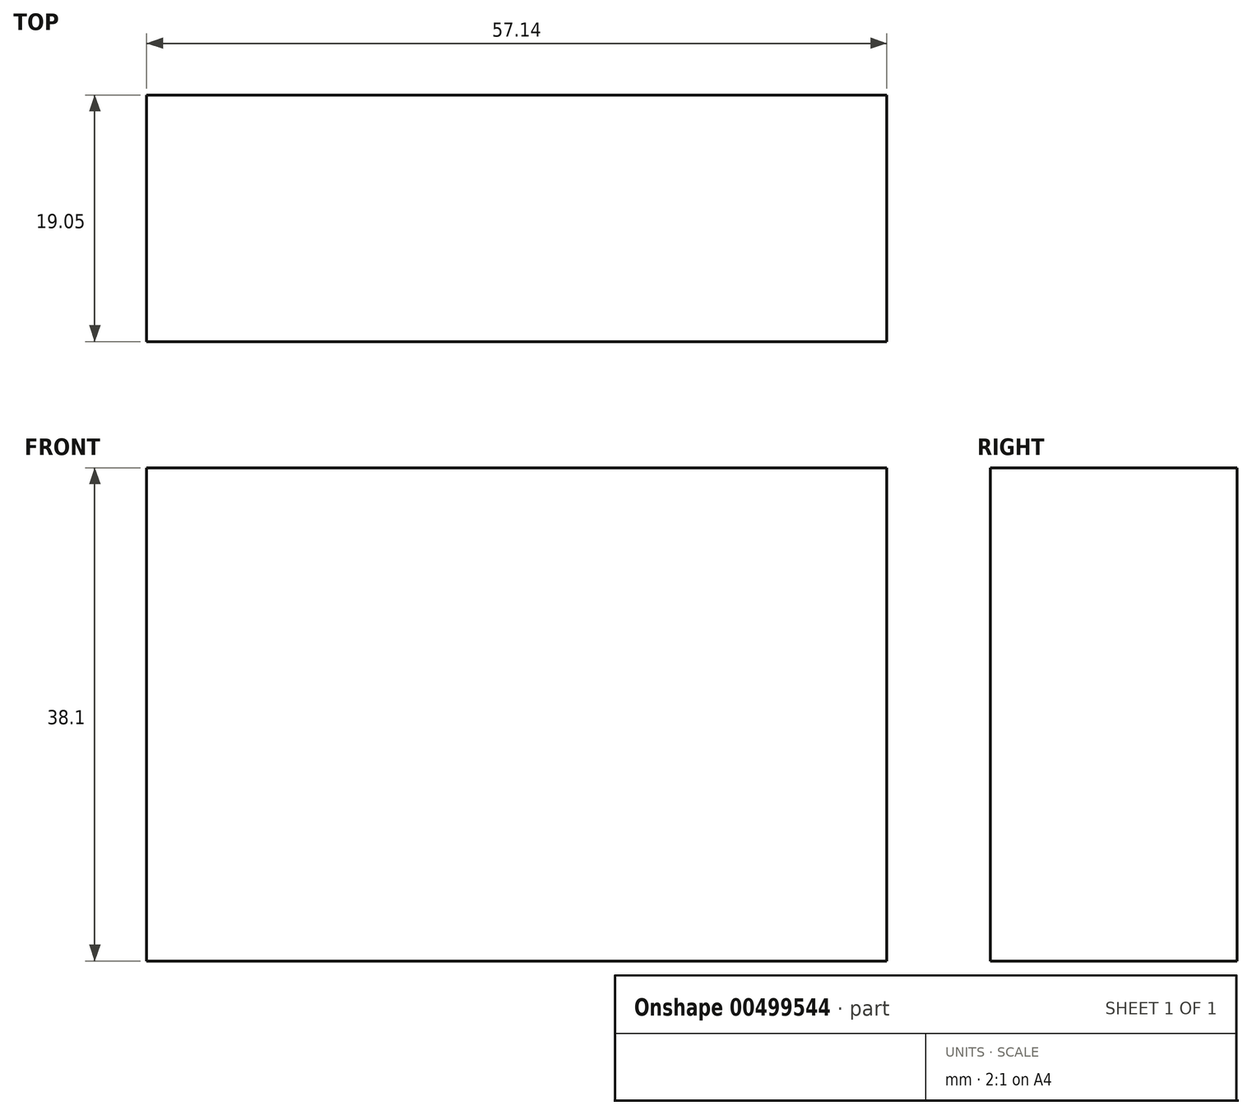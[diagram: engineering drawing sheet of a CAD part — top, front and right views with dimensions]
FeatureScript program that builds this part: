
annotation { "Feature Type Name" : "Feature", "Feature Type Description" : "" }
export const myFeature = defineFeature(function(context is Context, id is Id, definition is map)
    precondition{}
    {
        {
            var Q0;
            Q0=qCreatedBy(makeId("Top.planeOp"),FACE);
            var sketch = newSketch(context, id + "F0", { "sketchPlane" : qUnion([Q0])});
            skLineSegment(sketch, "E0.bottom", {"start": v(-28.58, 19.05) * mm, "end": v(28.58, 19.05) * mm});
            skLineSegment(sketch, "E0.top", {"start": v(-28.58, -19.05) * mm, "end": v(28.58, -19.05) * mm});
            skLineSegment(sketch, "E0.left", {"start": v(-28.58, 19.05) * mm, "end": v(-28.58, -19.05) * mm});
            skLineSegment(sketch, "E0.right", {"start": v(28.58, 19.05) * mm, "end": v(28.57, -19.05) * mm});
            skPoint(sketch, "E0.middle", {"position": v(0, 0) * mm});
            skLineSegment(sketch, "E1.bottom", {"start": v(28.58, -19.05) * mm, "end": v(9.52, -19.05) * mm});
            skLineSegment(sketch, "E1.top", {"start": v(28.58, 0) * mm, "end": v(9.52, 0) * mm});
            skLineSegment(sketch, "E1.left", {"start": v(28.58, -19.05) * mm, "end": v(28.58, 0) * mm});
            skLineSegment(sketch, "E1.right", {"start": v(9.52, -19.05) * mm, "end": v(9.52, 0) * mm});
            skLineSegment(sketch, "E2.bottom", {"start": v(9.52, 0) * mm, "end": v(-9.53, 0) * mm});
            skLineSegment(sketch, "E2.top", {"start": v(9.52, -19.05) * mm, "end": v(-9.53, -19.05) * mm});
            skLineSegment(sketch, "E2.left", {"start": v(9.52, 0) * mm, "end": v(9.52, -19.05) * mm});
            skLineSegment(sketch, "E2.right", {"start": v(-9.53, 0) * mm, "end": v(-9.53, -19.05) * mm});
            skLineSegment(sketch, "E3.bottom", {"start": v(-9.53, 0) * mm, "end": v(-28.58, 0) * mm});
            skLineSegment(sketch, "E3.top", {"start": v(-9.53, -19.05) * mm, "end": v(-28.58, -19.05) * mm});
            skLineSegment(sketch, "E3.right", {"start": v(-28.58, 0) * mm, "end": v(-28.58, -19.05) * mm});
            skLineSegment(sketch, "E4.bottom", {"start": v(-28.58, 0) * mm, "end": v(-9.53, 0) * mm});
            skLineSegment(sketch, "E4.top", {"start": v(-28.58, 19.05) * mm, "end": v(-9.53, 19.05) * mm});
            skLineSegment(sketch, "E4.left", {"start": v(-28.58, 0) * mm, "end": v(-28.58, 19.05) * mm});
            skLineSegment(sketch, "E4.right", {"start": v(-9.53, 0) * mm, "end": v(-9.53, 19.05) * mm});
            skLineSegment(sketch, "E5.bottom", {"start": v(-9.53, 19.05) * mm, "end": v(9.52, 19.05) * mm});
            skLineSegment(sketch, "E5.top", {"start": v(-9.53, 0) * mm, "end": v(9.52, 0) * mm});
            skLineSegment(sketch, "E5.left", {"start": v(-9.53, 19.05) * mm, "end": v(-9.53, 0) * mm});
            skLineSegment(sketch, "E5.right", {"start": v(9.52, 19.05) * mm, "end": v(9.52, 0) * mm});
            skSolve(sketch);
        }
        {
            var Q0;
            Q0=makeQuery(id+"F0.imprint","IMPRINT",FACE,{"disambiguationData":[TD([[makeQuery(id+"F0.imprint","IMPRINT",EDGE,{"derivedFrom":sQuery(id+"F0.wireOp",EDGE,"E3.top")}),-1.0]])]});
            var Q1;
            Q1=makeQuery(id+"F0.imprint","IMPRINT",FACE,{"disambiguationData":[TD([[makeQuery(id+"F0.imprint","IMPRINT",EDGE,{"derivedFrom":sQuery(id+"F0.wireOp",EDGE,"E4.bottom")}),1.0]])]});
            var Q2;
            Q2=makeQuery(id+"F0.imprint","IMPRINT",FACE,{"disambiguationData":[TD([[makeQuery(id+"F0.imprint","IMPRINT",EDGE,{"derivedFrom":sQuery(id+"F0.wireOp",EDGE,"E5.bottom")}),-1.0]])]});
            var Q3;
            Q3=makeQuery(id+"F0.imprint","IMPRINT",FACE,{"disambiguationData":[TD([[makeQuery(id+"F0.imprint","IMPRINT",EDGE,{"derivedFrom":sQuery(id+"F0.wireOp",EDGE,"E1.bottom")}),-1.0]])]});
            var Q4;
            Q4=makeQuery(id+"F0.imprint","IMPRINT",FACE,{"disambiguationData":[TD([[makeQuery(id+"F0.imprint","IMPRINT",EDGE,{"derivedFrom":sQuery(id+"F0.wireOp",EDGE,"E0.bottom")}),-1.0]])]});
            extrude(context, id + "F1", {"entities" : qUnion([Q0, Q1, Q2, Q3, Q4]), "depth" : 19.05 * mm});
        }
        {
            var Q0;
            Q0=makeQuery(id+"F0.imprint","IMPRINT",FACE,{"disambiguationData":[TD([[makeQuery(id+"F0.imprint","IMPRINT",EDGE,{"derivedFrom":sQuery(id+"F0.wireOp",EDGE,"E0.bottom")}),-1.0]])]});
            extrude(context, id + "F2", {"entities" : qUnion([Q0]), "operationType" : NewBodyOperationType.ADD, "depth" : 38.1 * mm});
        }
    });
